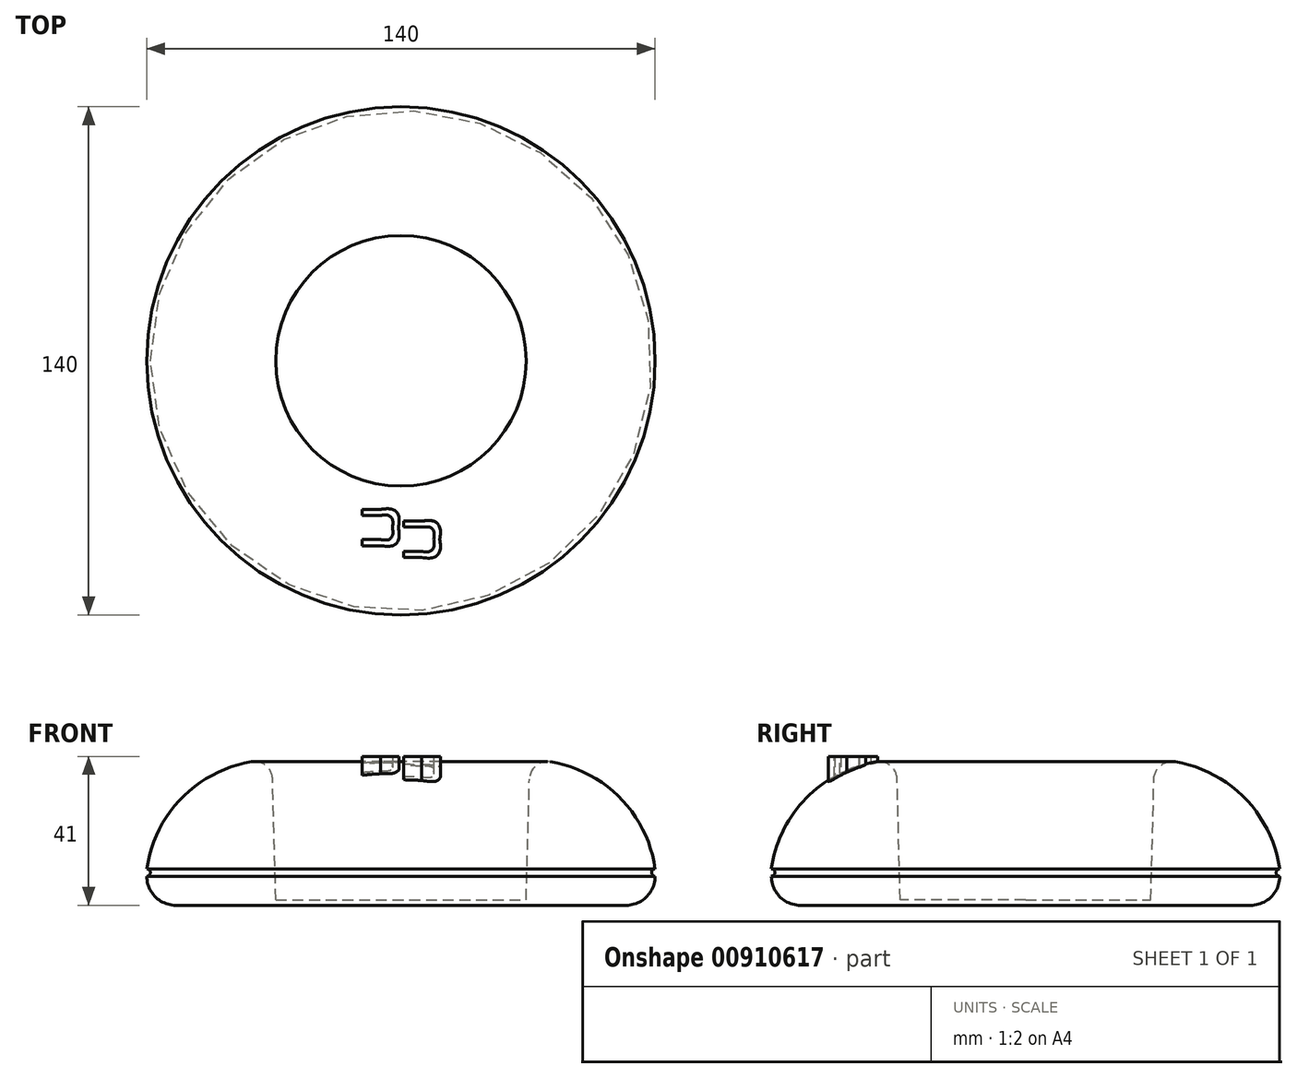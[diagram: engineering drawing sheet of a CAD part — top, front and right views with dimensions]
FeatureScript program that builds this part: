
annotation { "Feature Type Name" : "Feature", "Feature Type Description" : "" }
export const myFeature = defineFeature(function(context is Context, id is Id, definition is map)
    precondition{}
    {
        {
            var Q0;
            Q0=qCreatedBy(makeId("Front.planeOp"),FACE);
            var sketch = newSketch(context, id + "F0", { "sketchPlane" : qUnion([Q0])});
            skLineSegment(sketch, "E0.bottom", {"start": v(0, 0) * mm, "end": v(-62, 0) * mm});
            skLineSegment(sketch, "E0.left", {"start": v(0, 0) * mm, "end": v(0, 1.5) * mm});
            skLineSegment(sketch, "E1.top", {"start": v(0, 1.5) * mm, "end": v(-34.5, 1.5) * mm});
            skLineSegment(sketch, "E2", {"start": v(-70, 10) * mm, "end": v(-48.37, 10) * mm, "construction": true});
            skArc(sketch, "E3", {"start": v(-35.5, 40) * mm, "mid": v(-58.36, 31.45) * mm, "end": v(-70, 10) * mm});
            skLineSegment(sketch, "E4", {"start": v(-70, 9) * mm, "end": v(-50.44, 9) * mm, "construction": true});
            skArc(sketch, "E5", {"start": v(-70, 8) * mm, "mid": v(-69, 9) * mm, "end": v(-70, 10) * mm});
            skLineSegment(sketch, "E6", {"start": v(-62, 0) * mm, "end": v(-62, 6.86) * mm, "construction": true});
            skArc(sketch, "E7", {"start": v(-70, 8) * mm, "mid": v(-67.66, 2.34) * mm, "end": v(-62, 0) * mm});
            skPoint(sketch, "E8.orphan", {"position": v(-70, 0) * mm});
            skLineSegment(sketch, "E9", {"start": v(-35.5, 40) * mm, "end": v(-34.5, 1.5) * mm});
            skPoint(sketch, "E10.orphan", {"position": v(-35.5, 1.5) * mm});
            skSolve(sketch);
        }
        {
            var Q0;
            Q0=makeQuery(id+"F0.imprint","IMPRINT",FACE,{"disambiguationData":[TD([[makeQuery(id+"F0.imprint","IMPRINT",EDGE,{"derivedFrom":sQuery(id+"F0.wireOp",EDGE,"E0.bottom")}),-1.0]])]});
            var Q1;
            Q1=sQuery(id+"F0.wireOp",EDGE,"E0.left");
            revolve(context, id + "F1", {"surfaceOperationType" : NewSurfaceOperationType.NEW, "entities" : qUnion([Q0]), "axis" : qUnion([Q1]), "revolveType" : RevolveType.FULL});
        }
        {
            var Q0;
            Q0=makeQuery(id+"F1.opRevolve","SWEPT_EDGE",EDGE,{"disambiguationData":[OSD([sQuery(id+"F0.wireOp",EDGE,"E3"),sQuery(id+"F0.wireOp",EDGE,"E9")])]});
            fillet(context, id + "F2", {"entities" : qUnion([Q0]), "radius" : 5 * mm, "tangentPropagation" : true, "allowEdgeOverflow" : false});
        }
        {
            var Q0;
            Q0=qCreatedBy(makeId("Top.planeOp"),FACE);
            var sketch = newSketch(context, id + "F3", { "sketchPlane" : qUnion([Q0])});
            skLineSegment(sketch, "E11", {"start": v(-5.67, -42.6) * mm, "end": v(-10.67, -42.6) * mm});
            skLineSegment(sketch, "E12", {"start": v(-10.67, -42.6) * mm, "end": v(-10.67, -40.93) * mm});
            skLineSegment(sketch, "E13", {"start": v(-10.67, -40.93) * mm, "end": v(-5.67, -40.93) * mm});
            skLineSegment(sketch, "E14", {"start": v(-5.67, -50.93) * mm, "end": v(-10.67, -50.93) * mm});
            skLineSegment(sketch, "E15", {"start": v(-10.67, -50.93) * mm, "end": v(-10.67, -49.26) * mm});
            skLineSegment(sketch, "E16", {"start": v(-10.67, -49.26) * mm, "end": v(-5.67, -49.26) * mm});
            skFitSpline(sketch, "E17", {"points": [v(-5.67, -40.93) * mm, v(-2.34, -40.93) * mm, v(-0.67, -42.6) * mm, v(-0.67, -45.93) * mm]});
            skFitSpline(sketch, "E18", {"points": [v(-0.67, -45.93) * mm, v(-0.67, -49.26) * mm, v(-2.34, -50.93) * mm, v(-5.67, -50.93) * mm]});
            skFitSpline(sketch, "E19", {"points": [v(-5.67, -49.26) * mm, v(-3.45, -49.26) * mm, v(-2.34, -48.15) * mm, v(-2.34, -45.93) * mm]});
            skFitSpline(sketch, "E20", {"points": [v(-2.34, -45.93) * mm, v(-2.34, -43.7) * mm, v(-3.45, -42.6) * mm, v(-5.67, -42.6) * mm]});
            skLineSegment(sketch, "E21", {"start": v(5.69, -45.84) * mm, "end": v(0.69, -45.84) * mm});
            skLineSegment(sketch, "E22", {"start": v(0.69, -45.84) * mm, "end": v(0.69, -44.17) * mm});
            skLineSegment(sketch, "E23", {"start": v(0.69, -44.17) * mm, "end": v(5.69, -44.17) * mm});
            skLineSegment(sketch, "E24", {"start": v(5.69, -54.17) * mm, "end": v(0.69, -54.17) * mm});
            skLineSegment(sketch, "E25", {"start": v(0.69, -54.17) * mm, "end": v(0.69, -52.5) * mm});
            skLineSegment(sketch, "E26", {"start": v(0.69, -52.5) * mm, "end": v(5.69, -52.5) * mm});
            skFitSpline(sketch, "E27", {"points": [v(5.69, -44.17) * mm, v(9.02, -44.17) * mm, v(10.69, -45.84) * mm, v(10.69, -49.17) * mm]});
            skFitSpline(sketch, "E28", {"points": [v(10.69, -49.17) * mm, v(10.69, -52.5) * mm, v(9.02, -54.17) * mm, v(5.69, -54.17) * mm]});
            skFitSpline(sketch, "E29", {"points": [v(5.69, -52.5) * mm, v(7.9, -52.5) * mm, v(9.02, -51.4) * mm, v(9.02, -49.17) * mm]});
            skFitSpline(sketch, "E30", {"points": [v(9.02, -49.17) * mm, v(9.02, -46.95) * mm, v(7.9, -45.84) * mm, v(5.69, -45.84) * mm]});
            skSolve(sketch);
        }
        {
            var Q0;
            Q0 = qSketchRegion(id + "F3", true);
            extrude(context, id + "F4", {"entities" : qUnion([Q0]), "operationType" : NewBodyOperationType.ADD, "depth" : 41 * mm, "offsetDistance" : 25 * mm});
        }
    });
